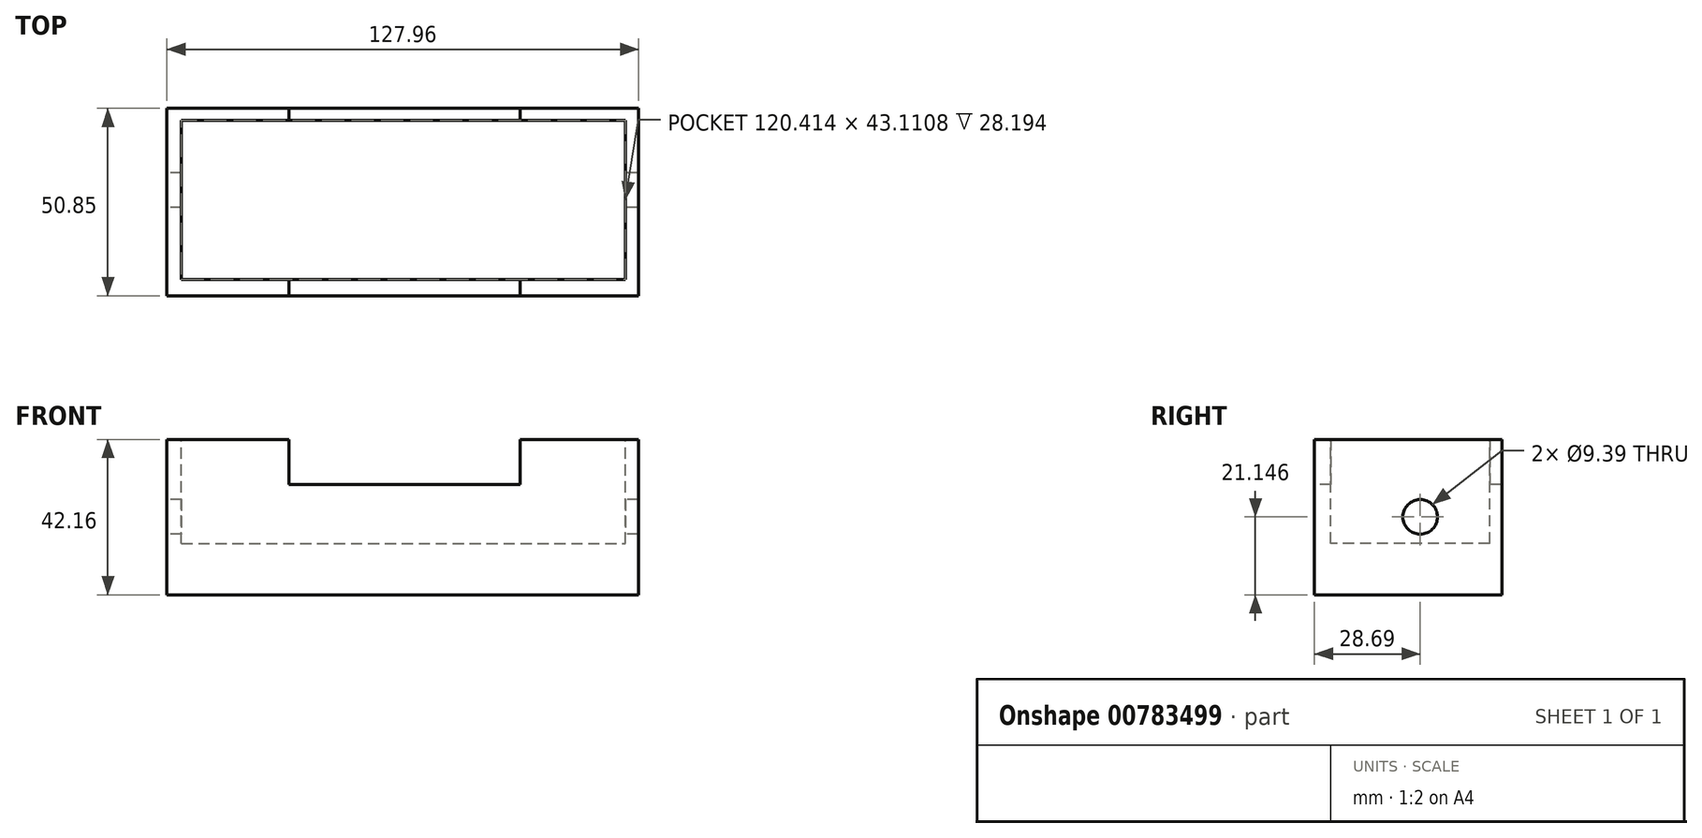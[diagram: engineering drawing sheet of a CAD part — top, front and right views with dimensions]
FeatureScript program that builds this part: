
annotation { "Feature Type Name" : "Feature", "Feature Type Description" : "" }
export const myFeature = defineFeature(function(context is Context, id is Id, definition is map)
    precondition{}
    {
        {
            var Q0;
            Q0=qCreatedBy(makeId("Top.planeOp"),FACE);
            var sketch = newSketch(context, id + "F0", { "sketchPlane" : qUnion([Q0])});
            skLineSegment(sketch, "E0.bottom", {"start": v(-64.22, 16.03) * mm, "end": v(63.74, 16.03) * mm});
            skLineSegment(sketch, "E0.top", {"start": v(-64.22, -34.82) * mm, "end": v(63.74, -34.82) * mm});
            skLineSegment(sketch, "E0.left", {"start": v(-64.22, 16.03) * mm, "end": v(-64.22, -34.82) * mm});
            skLineSegment(sketch, "E0.right", {"start": v(63.74, 16.03) * mm, "end": v(63.74, -34.82) * mm});
            skSolve(sketch);
        }
        {
            var Q0;
            Q0 = qSketchRegion(id + "F0", true);
            extrude(context, id + "F1", {"entities" : qUnion([Q0]), "depth" : 42.16 * mm, "offsetDistance" : 25.4 * mm});
        }
        {
            var Q0;
            Q0=makeQuery(id+"F1.opExtrude","SWEPT_FACE",FACE,{"disambiguationData":[OSD([sQuery(id+"F0.wireOp",EDGE,"E0.top")])]});
            var sketch = newSketch(context, id + "F2", { "sketchPlane" : qUnion([Q0])});
            skLineSegment(sketch, "E1", {"start": v(-31.14, 42.16) * mm, "end": v(-31.14, 29.95) * mm});
            skLineSegment(sketch, "E2", {"start": v(-31.14, 29.95) * mm, "end": v(31.61, 29.95) * mm});
            skLineSegment(sketch, "E3", {"start": v(31.61, 29.95) * mm, "end": v(31.61, 42.16) * mm});
            skSolve(sketch);
        }
        {
            var Q0;
            Q0=makeQuery(id+"F1.opExtrude","CAP_FACE",FACE,{"disambiguationData":[OSD([sQuery(id+"F0.wireOp",EDGE,"E0.bottom"),sQuery(id+"F0.wireOp",EDGE,"E0.top"),sQuery(id+"F0.wireOp",EDGE,"E0.left"),sQuery(id+"F0.wireOp",EDGE,"E0.right")])],"isStart":false});
            var sketch = newSketch(context, id + "F3", { "sketchPlane" : qUnion([Q0])});
            skLineSegment(sketch, "E4.bottom", {"start": v(-60.27, 12.73) * mm, "end": v(60.15, 12.73) * mm});
            skLineSegment(sketch, "E4.top", {"start": v(-60.27, -30.38) * mm, "end": v(60.15, -30.38) * mm});
            skLineSegment(sketch, "E4.left", {"start": v(-60.27, 12.73) * mm, "end": v(-60.27, -30.38) * mm});
            skLineSegment(sketch, "E4.right", {"start": v(60.15, 12.73) * mm, "end": v(60.15, -30.38) * mm});
            skSolve(sketch);
        }
        {
            var Q0;
            Q0 = qSketchRegion(id + "F3", true);
            extrude(context, id + "F4", {"entities" : qUnion([Q0]), "operationType" : NewBodyOperationType.REMOVE, "oppositeDirection" : true, "depth" : 28.2 * mm, "offsetDistance" : 25.4 * mm});
        }
        {
            var Q0;
            Q0 = qSketchRegion(id + "F2", true);
            var Q1;
            {var subQ0=sQuery(id+"F2.wireOp",EDGE,"E1");Q1=makeQuery(id+"F2.imprint","IMPRINT",FACE,{"disambiguationData":[TD([[makeQuery(id+"F2.imprint","IMPRINT",EDGE,{"derivedFrom":subQ0}),1.0]])]});}
            extrude(context, id + "F5", {"entities" : qUnion([Q0, Q1]), "operationType" : NewBodyOperationType.REMOVE, "oppositeDirection" : true, "depth" : 61.47 * mm, "offsetDistance" : 25.4 * mm});
        }
        {
            var Q0;
            Q0=makeQuery(id+"F1.opExtrude","SWEPT_FACE",FACE,{"disambiguationData":[OSD([sQuery(id+"F0.wireOp",EDGE,"E0.left")])]});
            var sketch = newSketch(context, id + "F6", { "sketchPlane" : qUnion([Q0])});
            skCircle(sketch, "E5", {"center": v(6.13, 21.15) * mm, "radius": 4.7 * mm});
            skSolve(sketch);
        }
        {
            var Q0;
            Q0 = qSketchRegion(id + "F6", true);
            extrude(context, id + "F7", {"entities" : qUnion([Q0]), "operationType" : NewBodyOperationType.REMOVE, "oppositeDirection" : true, "depth" : 174.5 * mm, "offsetDistance" : 25.4 * mm});
        }
    });
